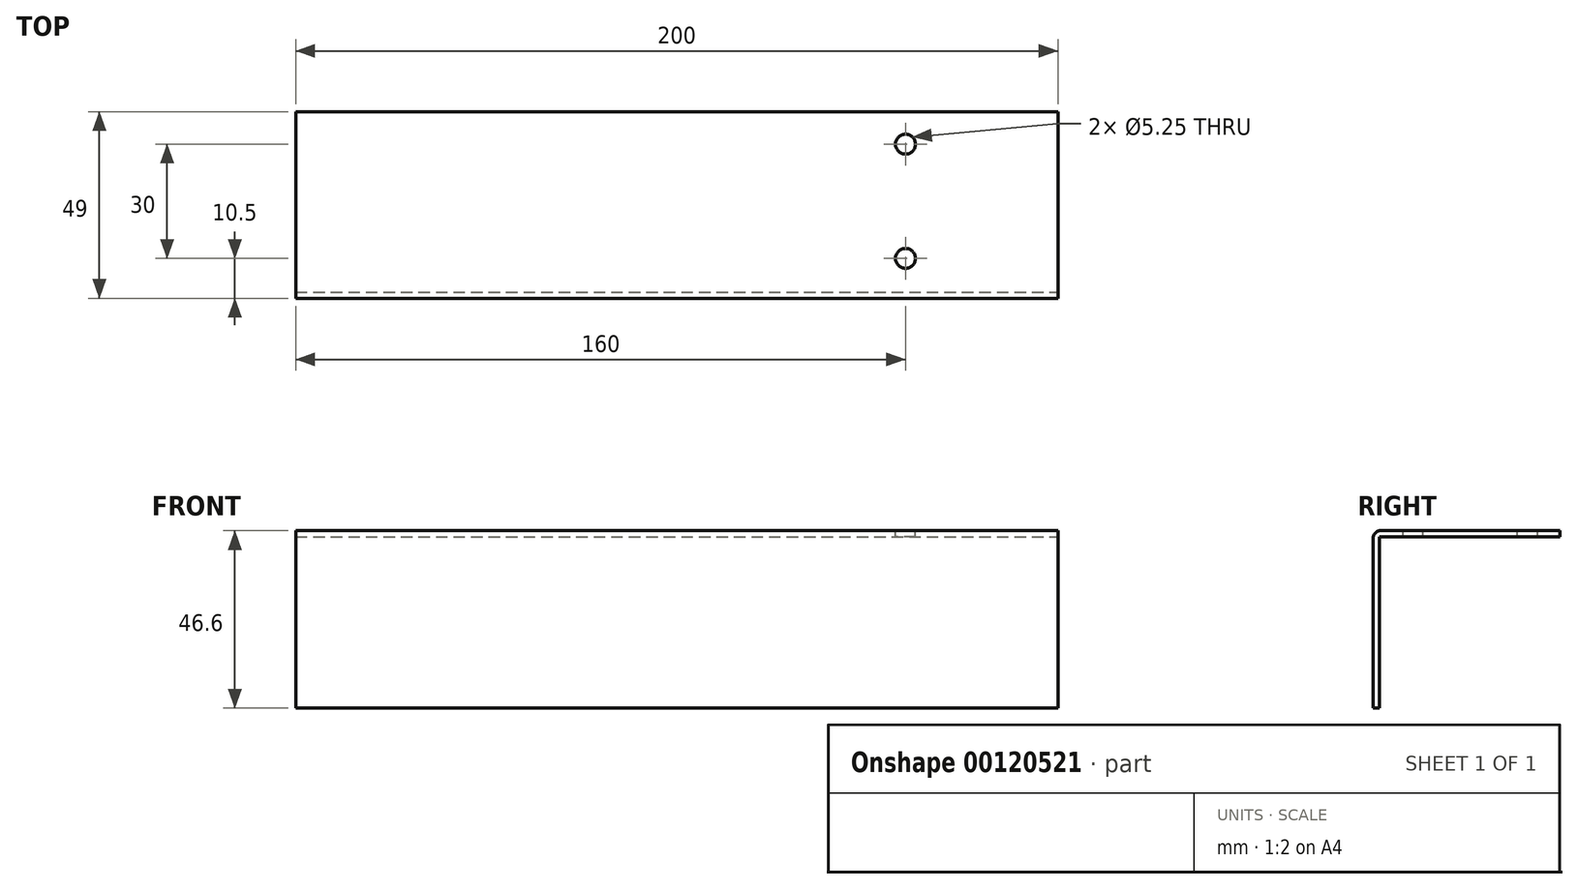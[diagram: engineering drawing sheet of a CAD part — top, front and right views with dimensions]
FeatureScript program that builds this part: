
annotation { "Feature Type Name" : "Feature", "Feature Type Description" : "" }
export const myFeature = defineFeature(function(context is Context, id is Id, definition is map)
    precondition{}
    {
        {
            var Q0;
            Q0=qCreatedBy(makeId("Top.planeOp"),FACE);
            var sketch = newSketch(context, id + "F0", { "sketchPlane" : qUnion([Q0])});
            skLineSegment(sketch, "E0.bottom", {"start": v(-100, 23.5) * mm, "end": v(100, 23.5) * mm});
            skLineSegment(sketch, "E0.top", {"start": v(-100, -25.5) * mm, "end": v(100, -25.5) * mm});
            skLineSegment(sketch, "E0.left", {"start": v(-100, 23.5) * mm, "end": v(-100, -25.5) * mm});
            skLineSegment(sketch, "E0.right", {"start": v(100, 23.5) * mm, "end": v(100, -25.5) * mm});
            skCircle(sketch, "E1", {"center": v(60, 15) * mm, "radius": 2.62 * mm});
            skCircle(sketch, "E2.MirrorC", {"center": v(60, -15) * mm, "radius": 2.62 * mm});
            skSolve(sketch);
        }
        {
            var Q0;
            Q0=makeQuery(id+"F0.imprint","IMPRINT",FACE,{"disambiguationData":[TD([[makeQuery(id+"F0.imprint","IMPRINT",EDGE,{"derivedFrom":sQuery(id+"F0.wireOp",EDGE,"E0.bottom")}),-1.0]])]});
            extrude(context, id + "F1", {"entities" : qUnion([Q0]), "oppositeDirection" : true, "depth" : 1.6 * mm, "offsetDistance" : 25 * mm});
        }
        {
            var Q0;
            Q0=makeQuery(id+"F1.opExtrude","CAP_FACE",FACE,{"disambiguationData":[OSD([sQuery(id+"F0.wireOp",EDGE,"E0.bottom"),sQuery(id+"F0.wireOp",EDGE,"E0.top"),sQuery(id+"F0.wireOp",EDGE,"E0.left"),sQuery(id+"F0.wireOp",EDGE,"E0.right"),sQuery(id+"F0.wireOp",EDGE,"E1"),sQuery(id+"F0.wireOp",EDGE,"E2.MirrorC")])],"isStart":false});
            var sketch = newSketch(context, id + "F2", { "sketchPlane" : qUnion([Q0])});
            skSolve(sketch);
        }
        {
            var Q0;
            Q0=makeQuery(id+"F2.imprint","IMPRINT",FACE,{"disambiguationData":[TD([[makeQuery(id+"F2.imprint","IMPRINT",EDGE,{"derivedFrom":makeQuery(id+"F1.opExtrude","CAP_EDGE",EDGE,{"disambiguationData":[OSD([sQuery(id+"F0.wireOp",EDGE,"E0.bottom")])],"isStart":false})}),1.0]])]});
            var sketch = newSketch(context, id + "F3", { "sketchPlane" : qUnion([Q0])});
            skLineSegment(sketch, "E3.bottom", {"start": v(-100, 25.5) * mm, "end": v(100, 25.5) * mm});
            skLineSegment(sketch, "E3.top", {"start": v(-100, 23.9) * mm, "end": v(100, 23.9) * mm});
            skLineSegment(sketch, "E3.left", {"start": v(-100, 25.5) * mm, "end": v(-100, 23.9) * mm});
            skLineSegment(sketch, "E3.right", {"start": v(100, 25.5) * mm, "end": v(100, 23.9) * mm});
            skSolve(sketch);
        }
        {
            var Q0;
            Q0=makeQuery(id+"F3.imprint","IMPRINT",FACE,{"disambiguationData":[TD([[makeQuery(id+"F3.imprint","IMPRINT",EDGE,{"derivedFrom":sQuery(id+"F3.wireOp",EDGE,"E3.bottom")}),-1.0]])]});
            extrude(context, id + "F4", {"entities" : qUnion([Q0]), "operationType" : NewBodyOperationType.ADD, "depth" : 45 * mm, "offsetDistance" : 25 * mm});
        }
        {
            var Q0;
            Q0=makeQuery(id+"F4.opExtrude","CAP_EDGE",EDGE,{"disambiguationData":[OSD([sQuery(id+"F3.wireOp",EDGE,"E3.top")])],"isStart":true});
            var Q1;
            Q1=makeQuery(id+"F1.opExtrude","CAP_EDGE",EDGE,{"disambiguationData":[OSD([sQuery(id+"F0.wireOp",EDGE,"E0.top")])],"isStart":true});
            fillet(context, id + "F5", {"entities" : qUnion([Q0, Q1]), "radius" : 2 * mm, "tangentPropagation" : true, "allowEdgeOverflow" : false});
        }
    });
